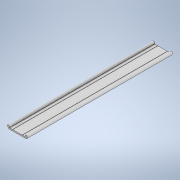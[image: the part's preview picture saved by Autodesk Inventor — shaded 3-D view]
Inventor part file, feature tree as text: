
AUTODESK INVENTOR PART (.ipt)
format: ipt  version: 2020 (Build 240168000, 168)  size: 137,216 bytes
history: native  units: mm
features: other x1, extrude x1, sketch x1
ambient origin geometry x8: Origin, YZ Plane, XZ Plane, XY Plane, X Axis, Y Axis, Z Axis, Center Point
bodies: Body1 (feature_tree)
feature tree (3):
  other  "Bryła1"
  extrude  "Wyciągnięcie proste1"  Depth=37.0mm
  sketch  "Szkic1"
